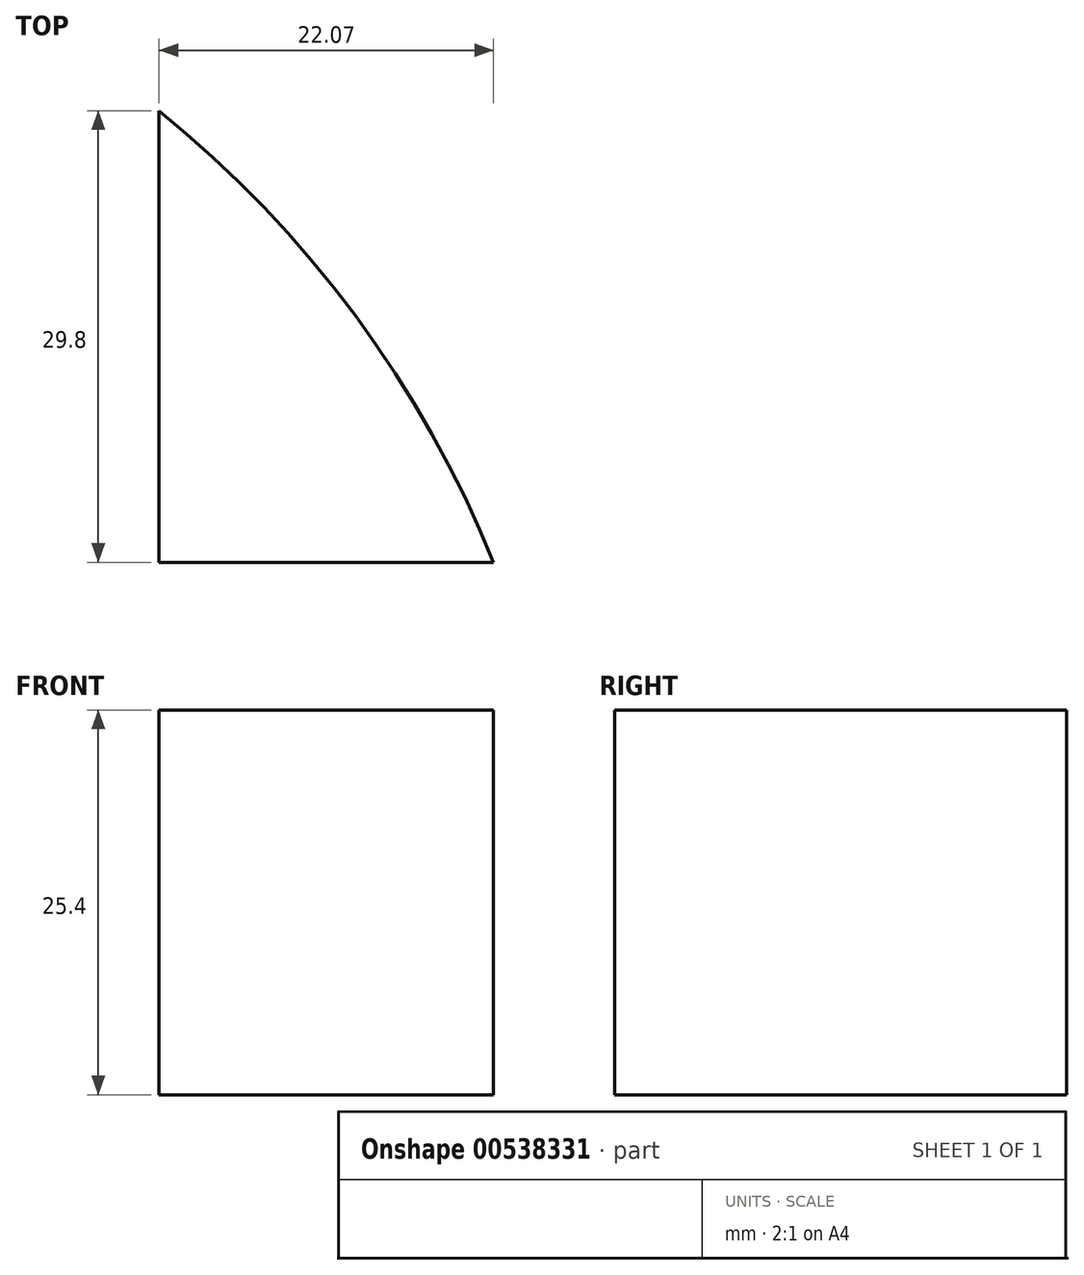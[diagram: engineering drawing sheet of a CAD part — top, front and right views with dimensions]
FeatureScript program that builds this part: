
annotation { "Feature Type Name" : "Feature", "Feature Type Description" : "" }
export const myFeature = defineFeature(function(context is Context, id is Id, definition is map)
    precondition{}
    {
        {
            var Q0;
            Q0=qCreatedBy(makeId("Top.planeOp"),FACE);
            var sketch = newSketch(context, id + "F0", { "sketchPlane" : qUnion([Q0])});
            skLineSegment(sketch, "E0", {"start": v(0, 0) * mm, "end": v(0, 29.8) * mm});
            skLineSegment(sketch, "E1", {"start": v(0, 0) * mm, "end": v(22.07, 0) * mm});
            skLineSegment(sketch, "E2", {"start": v(0, 0) * mm, "end": v(-22.07, 0) * mm});
            skPoint(sketch, "E2.endSnap0", {"position": v(11.04, 0) * mm});
            skArc(sketch, "E3", {"start": v(22.07, 0) * mm, "mid": v(13.05, 16.39) * mm, "end": v(0, 29.8) * mm});
            skArc(sketch, "E4", {"start": v(22.07, 0) * mm, "mid": v(12.93, 16.3) * mm, "end": v(0, 29.8) * mm});
            skSolve(sketch);
        }
        {
            var Q0;
            Q0=makeQuery(id+"F0.imprint","IMPRINT",FACE,{"disambiguationData":[TD([[makeQuery(id+"F0.imprint","IMPRINT",EDGE,{"derivedFrom":sQuery(id+"F0.wireOp",EDGE,"E0")}),-1.0]])]});
            extrude(context, id + "F1", {"entities" : qUnion([Q0]), "depth" : 25.4 * mm, "offsetDistance" : 25.4 * mm});
        }
    });
